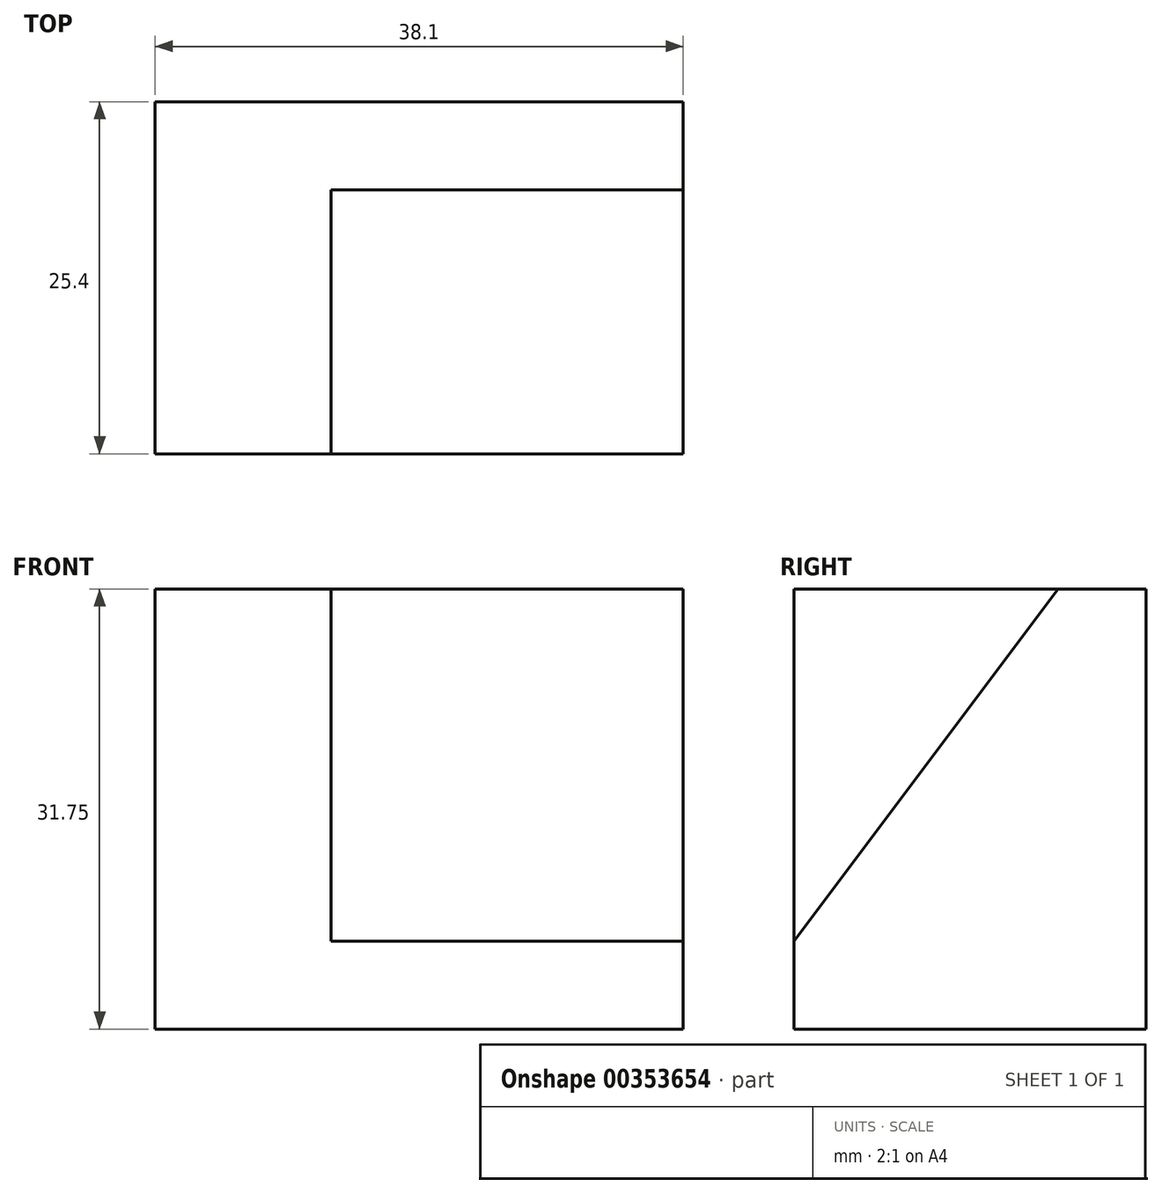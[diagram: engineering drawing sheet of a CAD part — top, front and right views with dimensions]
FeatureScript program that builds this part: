
annotation { "Feature Type Name" : "Feature", "Feature Type Description" : "" }
export const myFeature = defineFeature(function(context is Context, id is Id, definition is map)
    precondition{}
    {
        {
            var Q0;
            Q0=qCreatedBy(makeId("Front.planeOp"),FACE);
            var sketch = newSketch(context, id + "F0", { "sketchPlane" : qUnion([Q0])});
            skLineSegment(sketch, "E0", {"start": v(-16.44, 31.75) * mm, "end": v(-16.44, 0) * mm});
            skLineSegment(sketch, "E1", {"start": v(-16.44, 0) * mm, "end": v(21.66, 0) * mm});
            skLineSegment(sketch, "E2", {"start": v(21.66, 0) * mm, "end": v(21.66, 31.75) * mm});
            skLineSegment(sketch, "E3", {"start": v(21.66, 31.75) * mm, "end": v(-16.44, 31.75) * mm});
            skSolve(sketch);
        }
        {
            var Q0;
            Q0=makeQuery(id+"F0.imprint","IMPRINT",FACE,{"disambiguationData":[TD([[makeQuery(id+"F0.imprint","IMPRINT",EDGE,{"derivedFrom":sQuery(id+"F0.wireOp",EDGE,"E0")}),1.0]])]});
            extrude(context, id + "F1", {"entities" : qUnion([Q0]), "depth" : 25.4 * mm});
        }
        {
            var Q0;
            Q0=makeQuery(id+"F1.opExtrude","SWEPT_FACE",FACE,{"disambiguationData":[OSD([sQuery(id+"F0.wireOp",EDGE,"E2")])]});
            var sketch = newSketch(context, id + "F2", { "sketchPlane" : qUnion([Q0])});
            skLineSegment(sketch, "E4", {"start": v(-6.35, 31.75) * mm, "end": v(-25.4, 6.35) * mm});
            skSolve(sketch);
        }
        {
            var Q0;
            Q0 = qSketchRegion(id + "F2", true);
            var Q1;
            {var subQ0=sQuery(id+"F2.wireOp",EDGE,"E4");Q1=makeQuery(id+"F2.imprint","IMPRINT",FACE,{"disambiguationData":[TD([[makeQuery(id+"F2.imprint","IMPRINT",EDGE,{"derivedFrom":subQ0}),-1.0]])]});}
            extrude(context, id + "F3", {"entities" : qUnion([Q0, Q1]), "operationType" : NewBodyOperationType.REMOVE, "oppositeDirection" : true, "depth" : 25.4 * mm});
        }
    });
